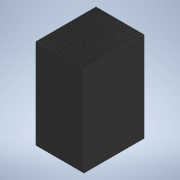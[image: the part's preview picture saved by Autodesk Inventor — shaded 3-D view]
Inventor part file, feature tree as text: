
AUTODESK INVENTOR PART (.ipt)
format: ipt  version: 2021 (Build 250183000, 183)  size: 107,008 bytes
history: native  units: mm
features: other x1, extrude x1, sketch x1
ambient origin geometry x8: Origin, YZ Plane, XZ Plane, XY Plane, X Axis, Y Axis, Z Axis, Center Point
bodies: Body1 (feature_tree)
feature tree (3):
  other  "Sólido1"
  extrude  "Extrusão1"  Depth=150.0mm
  sketch  "Esboço1"  dims[d0=80.0mm d1=150.0mm d2=100.0mm d3=0.0mm]
